# Revit family: Satellite-Dish
name_source: partatom
category: Specialty Equipment
units: mm (PartAtom-declared; Revit-internal decimal feet)

## family parameters
Always vertical = Yes
Cut with Voids When Loaded = No
Maintain Annotation Orientation = No
OmniClass Number = 23.85.50.27.17
OmniClass Title = Satellite Dishes
Part Type = Normal
Room Calculation Point = No
Round Connector Dimension = Use Diameter
Shared = No
Work Plane-Based = No

## types (1)
- Security-Camera
    Accent Color = Aluminum - Painted, Black
    Angle From Horizon = 22.50°
    Assembly Code = E1010100
    Bias = 30-200 mA
    Body Color = Aluminum - Painted, White
    Cabling = RG-6
    Construction Details = http://www.arcat.com
    Default Elevation = 0' - 0"
    Description = Security Camera
    Encoding = HDTV
    Expected Lifespan (Years) = 10
    Frame Color = Aluminum - Painted, Grey
    Green Building - LEED = http://www.arcat.com
    Keynote = 13700
    LNB = 5
    Maintenance Schedule (Months) = 0
    Manufacturer = Generic
    Manufacturer Fax = (203) 939-2444
    Manufacturer Website = http://www.arcat.com
    Max Receivers = 4
    Model = Generic
    Orbital Location = 110.00°
    Power Source = Line, 14.5V - 21V
    Product Data = http://www.arcat.com
    Product Properties = http://www.arcat.com
    Recording = DVR
    Satellite Reception = Ka99, Ka103, Ku101, Ku110, Ku119
    Show Range = Yes
    Specification = http://www.arcat.com
    Warranty Duration (Years) = 1
    anglsect = 11.25°

## geometry (parser evidence)
native form markers: Sweep x4
no freeform markers — native parametric forms only
